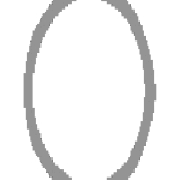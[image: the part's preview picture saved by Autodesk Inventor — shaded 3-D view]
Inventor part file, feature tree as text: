
AUTODESK INVENTOR PART (.ipt)
format: ipt  version: 2021 (Build 250183000, 183)  size: 110,080 bytes
history: native  units: in
note: dims shown in document units (in); Inventor stores cm internally (conversion verified against a paired STEP export)
features: other x4, sketch x3, plane x1
ambient origin geometry x8: Origin, YZ Plane, XZ Plane, XY Plane, X Axis, Y Axis, Z Axis, Center Point
bodies: Solid1 (feature_tree), Body (feature_tree)
feature tree (8):
  other  "Driven Length"
  other  "Frame Generator"
  other  "Start Plane"
  other  "End Plane"
  sketch  "Sketch"  dims[d2=14.6042in d4=-0.0in d5=14.6042in d6=0.12in d7=0.0in d8=90.0deg d9=14.6042in]
  sketch  "Sketch2"  dims[d0=1.0in]
  plane  "Work Plane3"
  sketch  "Sketch3"  dims[d1=0.065in]
